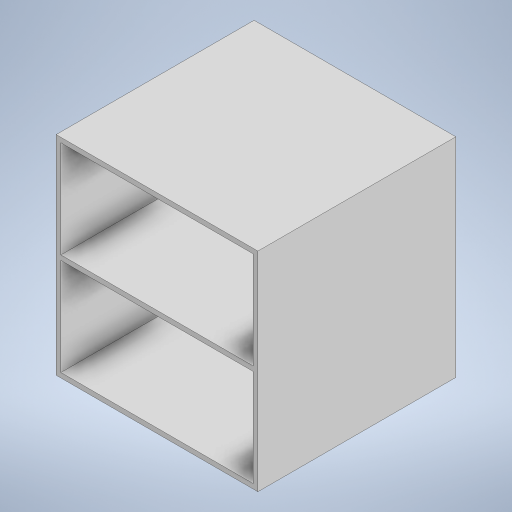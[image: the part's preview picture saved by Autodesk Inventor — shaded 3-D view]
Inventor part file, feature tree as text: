
AUTODESK INVENTOR PART (.ipt)
format: ipt  version: 2024 (Build 280153000, 153)  size: 206,336 bytes
history: native  units: mm
features: extrude x2, sketch x2
ambient origin geometry x8: Origin, YZ Plane, XZ Plane, XY Plane, X Axis, Y Axis, Z Axis, Center Point
bodies: Body1 (feature_tree)
feature tree (4):
  extrude  "Extrusion3"  Depth=106.0mm
  extrude  "Extrusion4"  Depth=104.0mm TaperAngle=0.0deg
  sketch  "Sketch1"  dims[d0=106.0mm d1=54.75mm]
  sketch  "Sketch4"  dims[d6=54.75mm d30=104.0mm d31=0.0mm d61=2.5mm d62=2.5mm d63=2.5mm d64=1.25mm d65=1.25mm d66=2.5mm d67=2.5mm d68=2.5mm d72=101.0mm d73=0.0mm]
